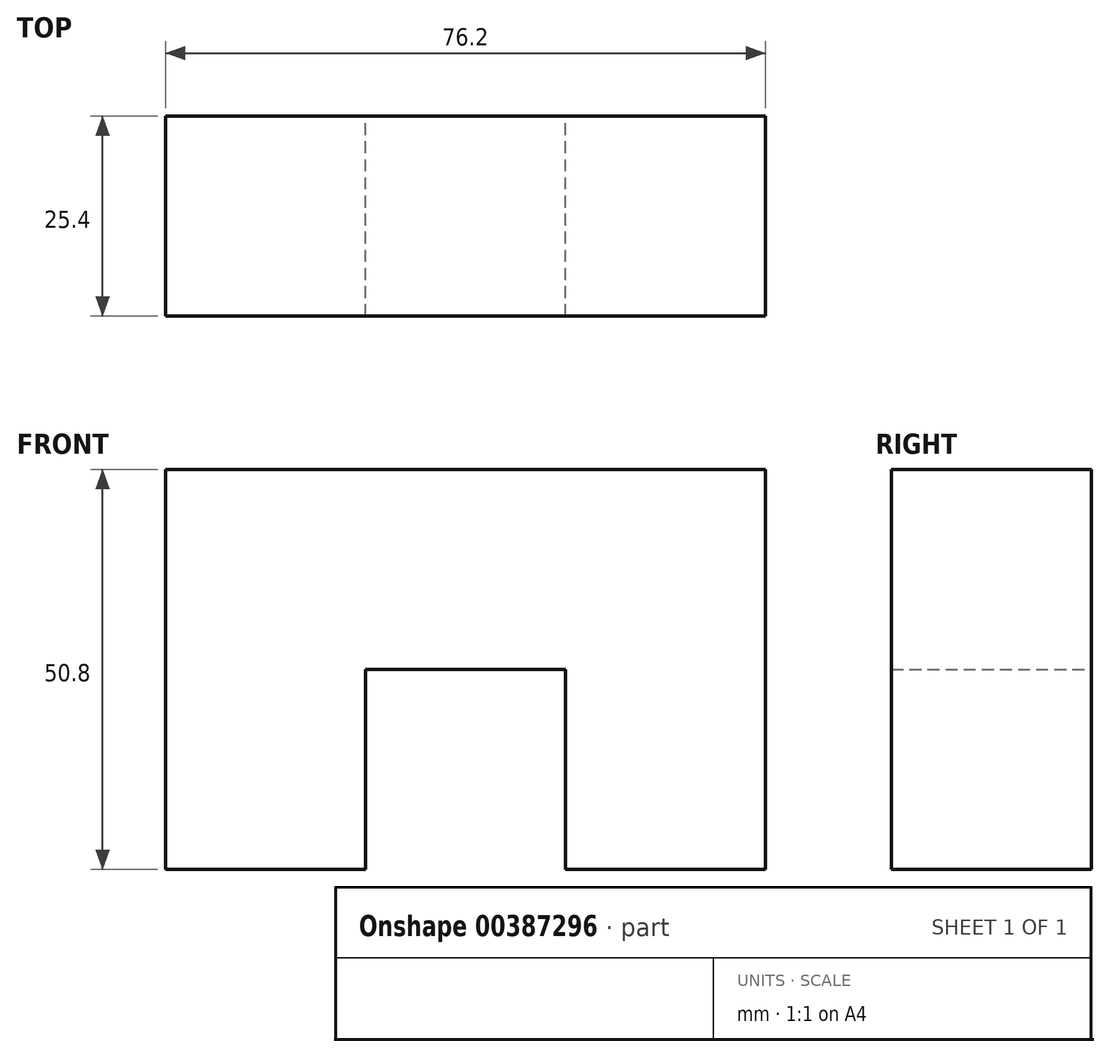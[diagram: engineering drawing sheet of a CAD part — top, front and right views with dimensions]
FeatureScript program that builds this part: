
annotation { "Feature Type Name" : "Feature", "Feature Type Description" : "" }
export const myFeature = defineFeature(function(context is Context, id is Id, definition is map)
    precondition{}
    {
        {
            var Q0;
            Q0=qCreatedBy(makeId("Front.planeOp"),FACE);
            var sketch = newSketch(context, id + "F0", { "sketchPlane" : qUnion([Q0])});
            skLineSegment(sketch, "E0.bottom", {"start": v(0, 0) * mm, "end": v(25.4, 0) * mm});
            skLineSegment(sketch, "E0.top", {"start": v(0, 25.4) * mm, "end": v(25.4, 25.4) * mm});
            skLineSegment(sketch, "E0.left", {"start": v(0, 0) * mm, "end": v(0, 25.4) * mm});
            skLineSegment(sketch, "E0.right", {"start": v(25.4, 0) * mm, "end": v(25.4, 25.4) * mm});
            skLineSegment(sketch, "E1.bottom", {"start": v(0, 0) * mm, "end": v(-25.4, 0) * mm});
            skLineSegment(sketch, "E1.top", {"start": v(0, 25.4) * mm, "end": v(-25.4, 25.4) * mm});
            skLineSegment(sketch, "E1.right", {"start": v(-25.4, 0) * mm, "end": v(-25.4, 25.4) * mm});
            skLineSegment(sketch, "E2.bottom", {"start": v(-25.4, 0) * mm, "end": v(0, 0) * mm});
            skLineSegment(sketch, "E2.top", {"start": v(-25.4, -25.4) * mm, "end": v(0, -25.4) * mm});
            skLineSegment(sketch, "E2.left", {"start": v(-25.4, 0) * mm, "end": v(-25.4, -25.4) * mm});
            skLineSegment(sketch, "E2.right", {"start": v(0, 0) * mm, "end": v(0, -25.4) * mm});
            skLineSegment(sketch, "E3.bottom", {"start": v(25.4, 25.4) * mm, "end": v(50.8, 25.4) * mm});
            skLineSegment(sketch, "E3.top", {"start": v(25.4, 0) * mm, "end": v(50.8, 0) * mm});
            skLineSegment(sketch, "E3.left", {"start": v(25.4, 25.4) * mm, "end": v(25.4, 0) * mm});
            skLineSegment(sketch, "E3.right", {"start": v(50.8, 25.4) * mm, "end": v(50.8, 0) * mm});
            skLineSegment(sketch, "E4.top", {"start": v(25.4, -25.4) * mm, "end": v(50.8, -25.4) * mm});
            skLineSegment(sketch, "E4.left", {"start": v(25.4, 0) * mm, "end": v(25.4, -25.4) * mm});
            skLineSegment(sketch, "E4.right", {"start": v(50.8, 0) * mm, "end": v(50.8, -25.4) * mm});
            skSolve(sketch);
        }
        {
            var Q0;
            Q0 = qSketchRegion(id + "F0", true);
            extrude(context, id + "F1", {"entities" : qUnion([Q0]), "depth" : 25.4 * mm});
        }
    });
